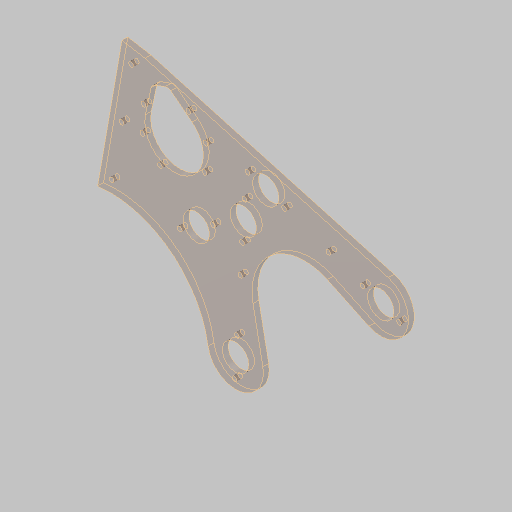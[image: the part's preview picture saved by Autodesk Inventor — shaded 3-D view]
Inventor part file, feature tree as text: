
AUTODESK INVENTOR PART (.ipt)
format: ipt  version: 2023.5 (Build 275446000, 446)  size: 433,664 bytes
history: native  units: in
note: dims shown in document units (in); Inventor stores cm internally (conversion verified against a paired STEP export)
features: sketch x3, extrude x2, hole x2, fillet x1, projected_geometry x1
ambient origin geometry x8: Origin, YZ Plane, XZ Plane, XY Plane, X Axis, Y Axis, Z Axis, Center Point
bodies: Solid1 (feature_tree)
feature tree (9):
  sketch  "Sketch1"  dims[d3=0.3489in d4=0.0in]
  extrude  "Extrusion1"  TaperAngle=0.0deg  [1 undecoded]
  hole  "Hole1"  [1 undecoded]
  hole  "Hole2"  [1 undecoded]
  extrude  "Extrusion2"  Depth=4.25in
  fillet  "Fillet1"  Radius=4.5in
  sketch  "Sketch2"  dims[d7=4.0in d8=4.0in]
  projected_geometry  "Projected Loop1"
  sketch  "Sketch3"  dims[d9=1.123in d10=4.0in d11=4.5in d12=4.5in d13=0.625in d14=0.625in d15=5.212in d16=1.128in d17=5.2115in d18=1.8765in d19=1.8765in d22=1.0in d23=6.0in d26=10.0585in d27=2.5in d30=8.0in d31=0.0687in d32=0.75in d33=4.75in d34=1.375in d35=0.75in d36=0.25in d38=2.3622in d40=360.0deg d44=0.375in d45=0.25in d46=0.0in d47=0.201in d48=0.75in d49=0.37in d50=0.25in d51=90.0deg d52=1.0in d53=0.8108in d55=0.5497in d56=0.3in d58=2.256in d59=2.5in d60=2.9555in d61=2.35in d62=0.3779in d65=2.0in d66=2.3622in d68=360.0deg d70=1.625in d71=60.0deg d72=1.655in d73=0.201in d74=0.75in d75=0.385in d76=0.25in d77=0.5635in d78=1.0in d79=0.8108in d80=1.75in d82=0.75in d83=0.0in d84=0.0in d85=0.25in d86=1.5748in d88=360.0deg d91=1.5748in d93=360.0deg d95=45.0deg d96=0.25in d97=0.825in d98=4.25in]
note: 3 required parameter values undecoded (feature->parameter linkage not recoverable at this tier; creation-order binding heuristic only, values carry confidence <= 0.55)
